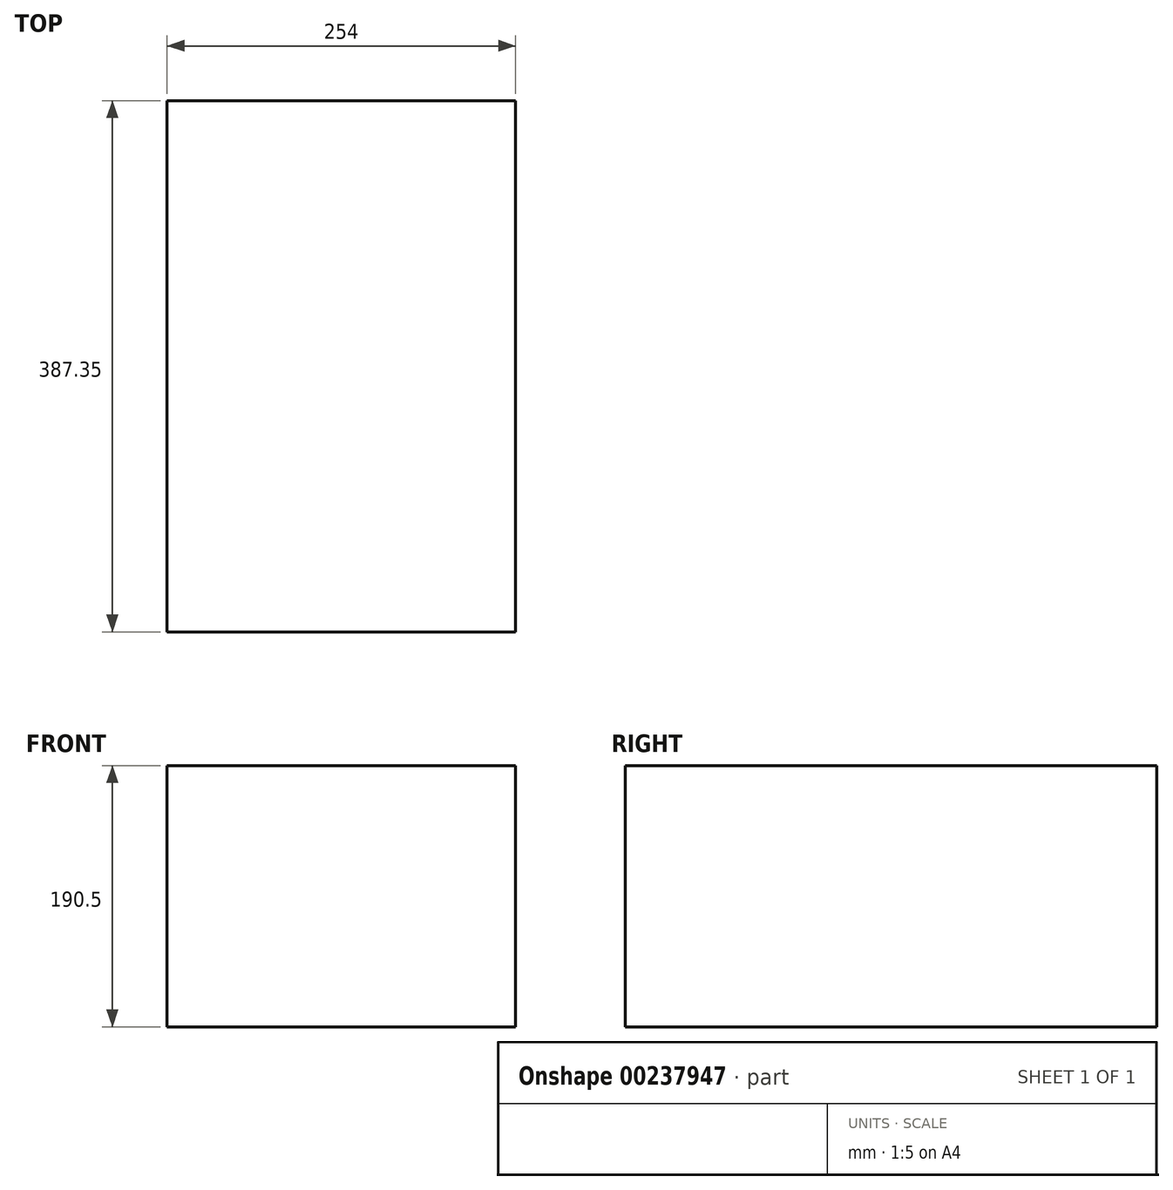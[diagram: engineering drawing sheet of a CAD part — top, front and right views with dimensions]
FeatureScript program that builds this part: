
annotation { "Feature Type Name" : "Feature", "Feature Type Description" : "" }
export const myFeature = defineFeature(function(context is Context, id is Id, definition is map)
    precondition{}
    {
        {
            var Q0;
            Q0=qCreatedBy(makeId("Top.planeOp"),FACE);
            var sketch = newSketch(context, id + "F0", { "sketchPlane" : qUnion([Q0])});
            skLineSegment(sketch, "E0.bottom", {"start": v(0, 0) * mm, "end": v(254, 0) * mm});
            skLineSegment(sketch, "E0.top", {"start": v(0, 387.35) * mm, "end": v(254, 387.35) * mm});
            skLineSegment(sketch, "E0.left", {"start": v(0, 0) * mm, "end": v(0, 387.35) * mm});
            skLineSegment(sketch, "E0.right", {"start": v(254, 0) * mm, "end": v(254, 387.35) * mm});
            skSolve(sketch);
        }
        {
            var Q0;
            Q0=makeQuery(id+"F0.imprint","IMPRINT",FACE,{"disambiguationData":[TD([[makeQuery(id+"F0.imprint","IMPRINT",EDGE,{"derivedFrom":sQuery(id+"F0.wireOp",EDGE,"E0.bottom")}),1.0]])]});
            extrude(context, id + "F1", {"entities" : qUnion([Q0]), "depth" : 190.5 * mm});
        }
    });
